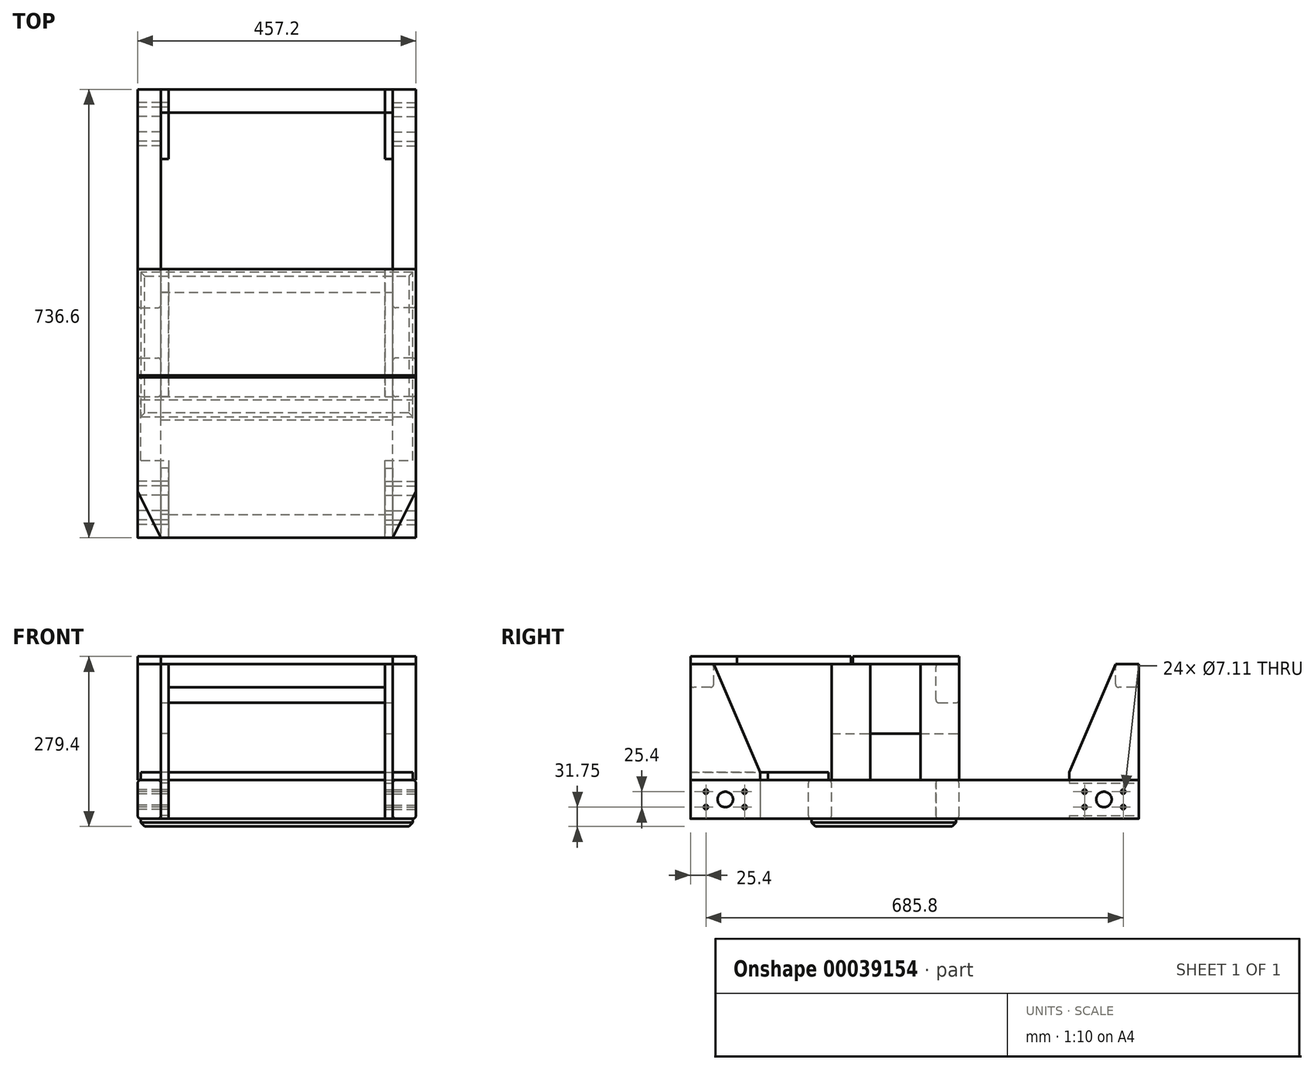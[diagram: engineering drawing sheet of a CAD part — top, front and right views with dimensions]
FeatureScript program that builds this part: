
annotation { "Feature Type Name" : "Feature", "Feature Type Description" : "" }
export const myFeature = defineFeature(function(context is Context, id is Id, definition is map)
    precondition{}
    {
        {
            var Q0;
            Q0=qCreatedBy(makeId("Front.planeOp"),FACE);
            var sketch = newSketch(context, id + "F0", { "sketchPlane" : qUnion([Q0])});
            skLineSegment(sketch, "E0", {"start": v(0, 25.4) * mm, "end": v(0, -25.4) * mm, "construction": true});
            skLineSegment(sketch, "E1.rect.bottom", {"start": v(-190.5, 31.75) * mm, "end": v(-228.6, 31.75) * mm});
            skLineSegment(sketch, "E1.rect.top", {"start": v(-190.5, -31.75) * mm, "end": v(-228.6, -31.75) * mm});
            skLineSegment(sketch, "E1.rect.left", {"start": v(-190.5, 31.75) * mm, "end": v(-190.5, -31.75) * mm});
            skLineSegment(sketch, "E1.rect.right", {"start": v(-228.6, 31.75) * mm, "end": v(-228.6, -31.75) * mm});
            skPoint(sketch, "E1.rect.middle", {"position": v(-209.55, 0) * mm});
            skLineSegment(sketch, "E2.MirrorCS", {"start": v(190.5, 31.75) * mm, "end": v(228.6, 31.75) * mm});
            skLineSegment(sketch, "E3.MirrorCS", {"start": v(190.5, -31.75) * mm, "end": v(228.6, -31.75) * mm});
            skLineSegment(sketch, "E4.MirrorCS", {"start": v(228.6, 31.75) * mm, "end": v(228.6, -31.75) * mm});
            skLineSegment(sketch, "E5.MirrorCS", {"start": v(190.5, 31.75) * mm, "end": v(190.5, -31.75) * mm});
            skPoint(sketch, "E6.MirrorP", {"position": v(209.55, 0) * mm});
            skSolve(sketch);
        }
        {
            var Q0;
            Q0=makeQuery(id+"F0.imprint","IMPRINT",FACE,{"disambiguationData":[TD([[makeQuery(id+"F0.imprint","IMPRINT",EDGE,{"derivedFrom":sQuery(id+"F0.wireOp",EDGE,"E1.rect.bottom")}),1.0]])]});
            extrude(context, id + "F1", {"entities" : qUnion([Q0]), "endBound" : BoundingType.SYMMETRIC, "depth" : 736.6 * mm});
        }
        {
            var Q0;
            Q0=makeQuery(id+"F1.opExtrude","SWEPT_FACE",FACE,{"disambiguationData":[OSD([sQuery(id+"F0.wireOp",EDGE,"E1.rect.right")])]});
            var sketch = newSketch(context, id + "F2", { "sketchPlane" : qUnion([Q0])});
            skLineSegment(sketch, "E7.rect.bottom", {"start": v(342.9, -12.7) * mm, "end": v(279.4, -12.7) * mm, "construction": true});
            skLineSegment(sketch, "E7.rect.top", {"start": v(342.9, 12.7) * mm, "end": v(279.4, 12.7) * mm, "construction": true});
            skLineSegment(sketch, "E7.rect.left", {"start": v(342.9, -12.7) * mm, "end": v(342.9, 12.7) * mm, "construction": true});
            skLineSegment(sketch, "E7.rect.right", {"start": v(279.4, -12.7) * mm, "end": v(279.4, 12.7) * mm, "construction": true});
            skPoint(sketch, "E7.rect.middle", {"position": v(311.15, 0) * mm});
            skCircle(sketch, "E8", {"center": v(311.15, 0) * mm, "radius": 12.7 * mm});
            skCircle(sketch, "E9", {"center": v(279.4, 12.7) * mm, "radius": 3.56 * mm});
            skCircle(sketch, "E10", {"center": v(279.4, -12.7) * mm, "radius": 3.56 * mm});
            skCircle(sketch, "E11", {"center": v(342.9, -12.7) * mm, "radius": 3.56 * mm});
            skCircle(sketch, "E12", {"center": v(342.9, 12.7) * mm, "radius": 3.56 * mm});
            skLineSegment(sketch, "E13", {"start": v(0, 31.75) * mm, "end": v(0, -31.75) * mm, "construction": true});
            skCircle(sketch, "E14.MirrorC", {"center": v(-342.9, 12.7) * mm, "radius": 3.56 * mm});
            skCircle(sketch, "E15.MirrorC", {"center": v(-342.9, -12.7) * mm, "radius": 3.56 * mm});
            skCircle(sketch, "E16.MirrorC", {"center": v(-279.4, 12.7) * mm, "radius": 3.56 * mm});
            skCircle(sketch, "E17.MirrorC", {"center": v(-279.4, -12.7) * mm, "radius": 3.56 * mm});
            skCircle(sketch, "E18.MirrorC", {"center": v(-311.15, 0) * mm, "radius": 12.7 * mm});
            skSolve(sketch);
        }
        {
            var Q0;
            Q0=qSketchRegion(id+"F2",true);
            extrude(context, id + "F3", {"entities" : qUnion([Q0]), "operationType" : NewBodyOperationType.REMOVE, "endBound" : BoundingType.THROUGH_ALL, "oppositeDirection" : true, "depth" : 25.4 * mm});
        }
        {
            var Q0;
            Q0=makeQuery(id+"F1.opExtrude","SWEPT_EDGE",EDGE,{"disambiguationData":[OSD([sQuery(id+"F0.wireOp",EDGE,"E1.rect.bottom"),sQuery(id+"F0.wireOp",EDGE,"E1.rect.right")])]});
            var Q1;
            Q1=makeQuery(id+"F1.opExtrude","SWEPT_EDGE",EDGE,{"disambiguationData":[OSD([sQuery(id+"F0.wireOp",EDGE,"E1.rect.bottom"),sQuery(id+"F0.wireOp",EDGE,"E1.rect.left")])]});
            var Q2;
            Q2=makeQuery(id+"F1.opExtrude","SWEPT_EDGE",EDGE,{"disambiguationData":[OSD([sQuery(id+"F0.wireOp",EDGE,"E1.rect.top"),sQuery(id+"F0.wireOp",EDGE,"E1.rect.right")])]});
            var Q3;
            Q3=makeQuery(id+"F1.opExtrude","SWEPT_EDGE",EDGE,{"disambiguationData":[OSD([sQuery(id+"F0.wireOp",EDGE,"E1.rect.top"),sQuery(id+"F0.wireOp",EDGE,"E1.rect.left")])]});
            fillet(context, id + "F4", {"entities" : qUnion([Q0, Q1, Q2, Q3]), "radius" : 5.08 * mm, "tangentPropagation" : true, "allowEdgeOverflow" : false});
        }
        {
            var Q0;
            Q0=makeQuery(id+"F1.opExtrude","SWEPT_BODY",BODY,{"disambiguationData":[OSD([sQuery(id+"F0.wireOp",EDGE,"E1.rect.bottom"),sQuery(id+"F0.wireOp",EDGE,"E1.rect.top"),sQuery(id+"F0.wireOp",EDGE,"E1.rect.left"),sQuery(id+"F0.wireOp",EDGE,"E1.rect.right")])]});
            var Q1;
            Q1=qCreatedBy(makeId("Right.planeOp"),FACE);
            mirror(context, id + "F5", {"entities" : qUnion([Q0]), "mirrorPlane" : qUnion([Q1])});
        }
        {
            var Q0;
            Q0=makeQuery(id+"F1.opExtrude","SWEPT_FACE",FACE,{"disambiguationData":[OSD([sQuery(id+"F0.wireOp",EDGE,"E1.rect.bottom")])]});
            var sketch = newSketch(context, id + "F6", { "sketchPlane" : qUnion([Q0])});
            skLineSegment(sketch, "E19.bottom", {"start": v(-190.5, -174.62) * mm, "end": v(190.5, -174.62) * mm});
            skLineSegment(sketch, "E19.top", {"start": v(-190.5, -136.53) * mm, "end": v(190.5, -136.53) * mm});
            skLineSegment(sketch, "E19.left", {"start": v(-190.5, -174.62) * mm, "end": v(-190.5, -136.53) * mm});
            skLineSegment(sketch, "E19.right", {"start": v(190.5, -174.62) * mm, "end": v(190.5, -136.53) * mm});
            skLineSegment(sketch, "E20", {"start": v(-190.5, -50.8) * mm, "end": v(190.5, -50.8) * mm, "construction": true});
            skLineSegment(sketch, "E21.MirrorCS", {"start": v(-190.5, 73.02) * mm, "end": v(190.5, 73.02) * mm});
            skLineSegment(sketch, "E22.MirrorCS", {"start": v(-190.5, 34.92) * mm, "end": v(190.5, 34.92) * mm});
            skLineSegment(sketch, "E23.MirrorCS", {"start": v(190.5, 73.02) * mm, "end": v(190.5, 34.92) * mm});
            skLineSegment(sketch, "E24.MirrorCS", {"start": v(-190.5, 73.02) * mm, "end": v(-190.5, 34.92) * mm});
            skSolve(sketch);
        }
        {
            var Q0;
            Q0=qSketchRegion(id+"F6",true);
            var Q1;
            Q1=makeQuery(id+"F5.opPattern","COPY",FACE,{"derivedFrom":makeQuery(id+"F1.opExtrude","SWEPT_FACE",FACE,{"disambiguationData":[OSD([sQuery(id+"F0.wireOp",EDGE,"E1.rect.top")])]}),"instanceName":"1"});
            extrude(context, id + "F7", {"entities" : qUnion([Q0]), "endBound" : BoundingType.UP_TO_SURFACE, "oppositeDirection" : true, "endBoundEntityFace" : qUnion([Q1]), "depth" : 25.4 * mm});
        }
        {
            var Q0;
            Q0=makeQuery(id+"F7.opExtrude","CAP_EDGE",EDGE,{"disambiguationData":[OSD([sQuery(id+"F6.wireOp",EDGE,"E21.MirrorCS")])],"isStart":false});
            var Q1;
            Q1=makeQuery(id+"F7.opExtrude","CAP_EDGE",EDGE,{"disambiguationData":[OSD([sQuery(id+"F6.wireOp",EDGE,"E22.MirrorCS")])],"isStart":false});
            var Q2;
            Q2=makeQuery(id+"F7.opExtrude","CAP_EDGE",EDGE,{"disambiguationData":[OSD([sQuery(id+"F6.wireOp",EDGE,"E19.top")])],"isStart":false});
            var Q3;
            Q3=makeQuery(id+"F7.opExtrude","CAP_EDGE",EDGE,{"disambiguationData":[OSD([sQuery(id+"F6.wireOp",EDGE,"E19.bottom")])],"isStart":false});
            var Q4;
            Q4=makeQuery(id+"F7.opExtrude","CAP_EDGE",EDGE,{"disambiguationData":[OSD([sQuery(id+"F6.wireOp",EDGE,"E19.bottom")])],"isStart":true});
            var Q5;
            Q5=makeQuery(id+"F7.opExtrude","CAP_EDGE",EDGE,{"disambiguationData":[OSD([sQuery(id+"F6.wireOp",EDGE,"E19.top")])],"isStart":true});
            var Q6;
            Q6=makeQuery(id+"F7.opExtrude","CAP_EDGE",EDGE,{"disambiguationData":[OSD([sQuery(id+"F6.wireOp",EDGE,"E22.MirrorCS")])],"isStart":true});
            var Q7;
            Q7=makeQuery(id+"F7.opExtrude","CAP_EDGE",EDGE,{"disambiguationData":[OSD([sQuery(id+"F6.wireOp",EDGE,"E21.MirrorCS")])],"isStart":true});
            fillet(context, id + "F8", {"entities" : qUnion([Q0, Q1, Q2, Q3, Q4, Q5, Q6, Q7]), "radius" : 5.08 * mm, "tangentPropagation" : true, "allowEdgeOverflow" : false});
        }
        {
            var Q0;
            Q0=makeQuery(id+"F1.opExtrude","SWEPT_FACE",FACE,{"disambiguationData":[OSD([sQuery(id+"F0.wireOp",EDGE,"E1.rect.bottom")])]});
            var sketch = newSketch(context, id + "F9", { "sketchPlane" : qUnion([Q0])});
            skLineSegment(sketch, "E25.bottom", {"start": v(-223.52, -241.3) * mm, "end": v(-177.8, -241.3) * mm});
            skLineSegment(sketch, "E25.top", {"start": v(-223.52, -141.6) * mm, "end": v(223.52, -141.6) * mm});
            skLineSegment(sketch, "E25.left", {"start": v(-223.52, -241.3) * mm, "end": v(-223.52, -141.6) * mm});
            skLineSegment(sketch, "E25.right", {"start": v(223.52, -241.3) * mm, "end": v(223.52, -141.6) * mm});
            skLineSegment(sketch, "E26.0", {"start": v(190.5, -141.6) * mm, "end": v(-190.5, -141.6) * mm, "construction": true});
            skLineSegment(sketch, "E27", {"start": v(-177.8, -241.3) * mm, "end": v(-177.8, -368.3) * mm});
            skLineSegment(sketch, "E28", {"start": v(-177.8, -368.3) * mm, "end": v(177.8, -368.3) * mm});
            skLineSegment(sketch, "E29", {"start": v(177.8, -368.3) * mm, "end": v(177.8, -241.3) * mm});
            skLineSegment(sketch, "E30", {"start": v(0, -141.6) * mm, "end": v(0, -368.3) * mm, "construction": true});
            skLineSegment(sketch, "E31.trimOffspring", {"start": v(177.8, -241.3) * mm, "end": v(223.52, -241.3) * mm});
            skSolve(sketch);
        }
        {
            var Q0;
            Q0=qSketchRegion(id+"F9",true);
            extrude(context, id + "F10", {"entities" : qUnion([Q0]), "depth" : 12.7 * mm});
        }
        {
            var Q0;
            Q0=makeQuery(id+"F5.opPattern","COPY",FACE,{"derivedFrom":makeQuery(id+"F1.opExtrude","SWEPT_FACE",FACE,{"disambiguationData":[OSD([sQuery(id+"F0.wireOp",EDGE,"E1.rect.top")])]}),"instanceName":"1"});
            var sketch = newSketch(context, id + "F11", { "sketchPlane" : qUnion([Q0])});
            skLineSegment(sketch, "E32.bottom", {"start": v(223.52, 169.55) * mm, "end": v(-223.52, 169.54) * mm});
            skLineSegment(sketch, "E32.top", {"start": v(223.52, -67.94) * mm, "end": v(-223.52, -67.95) * mm});
            skLineSegment(sketch, "E32.left", {"start": v(223.52, 169.55) * mm, "end": v(223.52, -67.94) * mm});
            skLineSegment(sketch, "E32.right", {"start": v(-223.52, 169.54) * mm, "end": v(-223.52, -67.95) * mm});
            skSolve(sketch);
        }
        {
            var Q0;
            Q0=qSketchRegion(id+"F11",true);
            extrude(context, id + "F12", {"entities" : qUnion([Q0]), "depth" : 12.7 * mm});
        }
        {
            var Q0;
            Q0=makeQuery(id+"F12.opExtrude","CAP_EDGE",EDGE,{"disambiguationData":[OSD([sQuery(id+"F11.wireOp",EDGE,"E32.top")])],"isStart":false});
            var Q1;
            Q1=makeQuery(id+"F12.opExtrude","CAP_EDGE",EDGE,{"disambiguationData":[OSD([sQuery(id+"F11.wireOp",EDGE,"E32.left")])],"isStart":false});
            var Q2;
            Q2=makeQuery(id+"F12.opExtrude","CAP_EDGE",EDGE,{"disambiguationData":[OSD([sQuery(id+"F11.wireOp",EDGE,"E32.bottom")])],"isStart":false});
            var Q3;
            Q3=makeQuery(id+"F12.opExtrude","CAP_EDGE",EDGE,{"disambiguationData":[OSD([sQuery(id+"F11.wireOp",EDGE,"E32.right")])],"isStart":false});
            chamfer(context, id + "F13", {"entities" : qUnion([Q0, Q1, Q2, Q3]), "width" : 6.35 * mm, "tangentPropagation" : true});
        }
        {
            var Q0;
            Q0=makeQuery(id+"F1.opExtrude","SWEPT_FACE",FACE,{"disambiguationData":[OSD([sQuery(id+"F0.wireOp",EDGE,"E1.rect.left")])]});
            var sketch = newSketch(context, id + "F14", { "sketchPlane" : qUnion([Q0])});
            skLineSegment(sketch, "E33", {"start": v(-254, -31.75) * mm, "end": v(-368.3, -31.75) * mm});
            skPoint(sketch, "E33.endSnap0", {"position": v(-368.3, 0) * mm});
            skLineSegment(sketch, "E34", {"start": v(-368.3, -31.75) * mm, "end": v(-368.3, 222.25) * mm});
            skLineSegment(sketch, "E35", {"start": v(-368.3, 222.25) * mm, "end": v(-330.2, 222.25) * mm});
            skLineSegment(sketch, "E36", {"start": v(-330.2, 222.25) * mm, "end": v(-254, 44.45) * mm});
            skLineSegment(sketch, "E37", {"start": v(-254, 44.45) * mm, "end": v(-254, -31.75) * mm});
            skLineSegment(sketch, "E38", {"start": v(0, -26.67) * mm, "end": v(0, 26.67) * mm, "construction": true});
            skLineSegment(sketch, "E39.MirrorCS", {"start": v(368.3, 222.25) * mm, "end": v(330.2, 222.25) * mm});
            skLineSegment(sketch, "E40.MirrorCS", {"start": v(254, -31.75) * mm, "end": v(368.3, -31.75) * mm});
            skPoint(sketch, "E41.MirrorP", {"position": v(368.3, 0) * mm});
            skLineSegment(sketch, "E42.MirrorCS", {"start": v(330.2, 222.25) * mm, "end": v(254, 44.45) * mm});
            skLineSegment(sketch, "E43.MirrorCS", {"start": v(254, 44.45) * mm, "end": v(254, -31.75) * mm});
            skLineSegment(sketch, "E44.MirrorCS", {"start": v(368.3, -31.75) * mm, "end": v(368.3, 222.25) * mm});
            skSolve(sketch);
        }
        {
            var Q0;
            {var subQ6=sQuery(id+"F14.wireOp",EDGE,"E35");Q0=makeQuery(id+"F14.imprint","IMPRINT",FACE,{"disambiguationData":[TD([[makeQuery(id+"F14.imprint","IMPRINT",EDGE,{"derivedFrom":subQ6}),-1.0]])]});}
            var Q1;
            {var subQ0=sQuery(id+"F0.wireOp",EDGE,"E1.rect.left");var subQ1=makeQuery(id+"F1.opExtrude","SWEPT_FACE",FACE,{"disambiguationData":[OSD([subQ0])]});Q1=makeQuery(id+"F14.imprint","IMPRINT",FACE,{"disambiguationData":[TD([[makeQuery(id+"F14.imprint","IMPRINT",EDGE,{"derivedFrom":makeQuery(id+"F3.boolean.opBoolean","INTERSECT",EDGE,{"derivedFrom":[subQ1,makeQuery(id+"F3.opExtrude","SWEPT_FACE",FACE,{"disambiguationData":[OSD([sQuery(id+"F2.wireOp",EDGE,"E8")])]})]})}),-1.0]])]});}
            var Q2;
            {var subQ4=sQuery(id+"F14.wireOp",EDGE,"E33");Q2=makeQuery(id+"F14.imprint","IMPRINT",FACE,{"disambiguationData":[TD([[makeQuery(id+"F14.imprint","IMPRINT",EDGE,{"derivedFrom":subQ4}),-1.0]])]});}
            var Q3;
            {var subQ0=sQuery(id+"F14.wireOp",EDGE,"E39.MirrorCS");Q3=makeQuery(id+"F14.imprint","IMPRINT",FACE,{"disambiguationData":[TD([[makeQuery(id+"F14.imprint","IMPRINT",EDGE,{"derivedFrom":subQ0}),1.0]])]});}
            var Q4;
            {var subQ0=sQuery(id+"F0.wireOp",EDGE,"E1.rect.left");var subQ1=makeQuery(id+"F1.opExtrude","SWEPT_FACE",FACE,{"disambiguationData":[OSD([subQ0])]});Q4=makeQuery(id+"F14.imprint","IMPRINT",FACE,{"disambiguationData":[TD([[makeQuery(id+"F14.imprint","IMPRINT",EDGE,{"derivedFrom":makeQuery(id+"F3.boolean.opBoolean","INTERSECT",EDGE,{"derivedFrom":[subQ1,makeQuery(id+"F3.opExtrude","SWEPT_FACE",FACE,{"disambiguationData":[OSD([sQuery(id+"F2.wireOp",EDGE,"E14.MirrorC")])]})]})}),1.0]])]});}
            var Q5;
            {var subQ6=sQuery(id+"F14.wireOp",EDGE,"E40.MirrorCS");Q5=makeQuery(id+"F14.imprint","IMPRINT",FACE,{"disambiguationData":[TD([[makeQuery(id+"F14.imprint","IMPRINT",EDGE,{"derivedFrom":subQ6}),1.0]])]});}
            extrude(context, id + "F15", {"entities" : qUnion([Q0, Q1, Q2, Q3, Q4, Q5]), "depth" : 12.7 * mm});
        }
        {
            var Q0;
            Q0=makeQuery(id+"F1.opExtrude","SWEPT_FACE",FACE,{"disambiguationData":[OSD([sQuery(id+"F0.wireOp",EDGE,"E1.rect.bottom")])]});
            var sketch = newSketch(context, id + "F16", { "sketchPlane" : qUnion([Q0])});
            skLineSegment(sketch, "E45.bottom", {"start": v(-228.6, 73.02) * mm, "end": v(-190.5, 73.02) * mm});
            skLineSegment(sketch, "E45.top", {"start": v(-228.6, 9.52) * mm, "end": v(-190.5, 9.52) * mm});
            skLineSegment(sketch, "E45.left", {"start": v(-228.6, 73.02) * mm, "end": v(-228.6, 9.52) * mm});
            skLineSegment(sketch, "E45.right", {"start": v(-190.5, 73.02) * mm, "end": v(-190.5, 9.52) * mm});
            skLineSegment(sketch, "E46.bottom", {"start": v(-228.6, -136.53) * mm, "end": v(-190.5, -136.53) * mm});
            skLineSegment(sketch, "E46.top", {"start": v(-228.6, -73.03) * mm, "end": v(-190.5, -73.03) * mm});
            skLineSegment(sketch, "E46.left", {"start": v(-228.6, -136.53) * mm, "end": v(-228.6, -73.03) * mm});
            skLineSegment(sketch, "E46.right", {"start": v(-190.5, -136.53) * mm, "end": v(-190.5, -73.03) * mm});
            skSolve(sketch);
        }
        {
            var Q0;
            Q0=qSketchRegion(id+"F16",true);
            var Q1;
            Q1=makeQuery(id+"F15.opExtrude","SWEPT_FACE",FACE,{"disambiguationData":[OSD([sQuery(id+"F14.wireOp",EDGE,"E35")])]});
            extrude(context, id + "F17", {"entities" : qUnion([Q0]), "endBound" : BoundingType.UP_TO_SURFACE, "endBoundEntityFace" : qUnion([Q1]), "depth" : 25.4 * mm});
        }
        {
            var Q0;
            Q0=makeQuery(id+"F1.opExtrude","SWEPT_FACE",FACE,{"disambiguationData":[OSD([sQuery(id+"F0.wireOp",EDGE,"E1.rect.left")])]});
            var sketch = newSketch(context, id + "F18", { "sketchPlane" : qUnion([Q0])});
            skLineSegment(sketch, "E47", {"start": v(-136.53, -31.75) * mm, "end": v(-136.53, 107.95) * mm});
            skLineSegment(sketch, "E48", {"start": v(-136.53, 107.95) * mm, "end": v(73.02, 107.95) * mm});
            skLineSegment(sketch, "E49", {"start": v(73.02, 107.95) * mm, "end": v(73.02, 31.75) * mm});
            skLineSegment(sketch, "E50", {"start": v(73.02, 31.75) * mm, "end": v(34.92, 31.75) * mm});
            skLineSegment(sketch, "E51", {"start": v(34.92, 31.75) * mm, "end": v(34.92, -31.75) * mm});
            skLineSegment(sketch, "E52", {"start": v(34.92, -31.75) * mm, "end": v(-136.53, -31.75) * mm});
            skSolve(sketch);
        }
        {
            var Q0;
            Q0=qSketchRegion(id+"F18",true);
            extrude(context, id + "F19", {"entities" : qUnion([Q0]), "depth" : 12.7 * mm});
        }
        {
            var Q0;
            Q0=makeQuery(id+"F15.opExtrude","SWEPT_BODY",BODY,{"disambiguationData":[OSD([sQuery(id+"F0.wireOp",EDGE,"E1.rect.left"),sQuery(id+"F2.wireOp",EDGE,"E8"),sQuery(id+"F2.wireOp",EDGE,"E9"),sQuery(id+"F2.wireOp",EDGE,"E10"),sQuery(id+"F2.wireOp",EDGE,"E11"),sQuery(id+"F2.wireOp",EDGE,"E12"),sQuery(id+"F14.wireOp",EDGE,"E33"),sQuery(id+"F14.wireOp",EDGE,"E34"),sQuery(id+"F14.wireOp",EDGE,"E35"),sQuery(id+"F14.wireOp",EDGE,"E36"),sQuery(id+"F14.wireOp",EDGE,"E37")])]});
            var Q1;
            Q1=makeQuery(id+"F17.opExtrude","SWEPT_BODY",BODY,{"disambiguationData":[OSD([sQuery(id+"F16.wireOp",EDGE,"E46.bottom"),sQuery(id+"F16.wireOp",EDGE,"E46.top"),sQuery(id+"F16.wireOp",EDGE,"E46.left"),sQuery(id+"F16.wireOp",EDGE,"E46.right")])]});
            var Q2;
            Q2=makeQuery(id+"F19.opExtrude","SWEPT_BODY",BODY,{"disambiguationData":[OSD([sQuery(id+"F18.wireOp",EDGE,"E47"),sQuery(id+"F18.wireOp",EDGE,"E48"),sQuery(id+"F18.wireOp",EDGE,"E49"),sQuery(id+"F18.wireOp",EDGE,"E50"),sQuery(id+"F18.wireOp",EDGE,"E51"),sQuery(id+"F18.wireOp",EDGE,"E52")])]});
            var Q3;
            Q3=makeQuery(id+"F17.opExtrude","SWEPT_BODY",BODY,{"disambiguationData":[OSD([sQuery(id+"F16.wireOp",EDGE,"E45.bottom"),sQuery(id+"F16.wireOp",EDGE,"E45.top"),sQuery(id+"F16.wireOp",EDGE,"E45.left"),sQuery(id+"F16.wireOp",EDGE,"E45.right")])]});
            var Q4;
            Q4=makeQuery(id+"F15.opExtrude","SWEPT_BODY",BODY,{"disambiguationData":[OSD([sQuery(id+"F0.wireOp",EDGE,"E1.rect.left"),sQuery(id+"F2.wireOp",EDGE,"E14.MirrorC"),sQuery(id+"F2.wireOp",EDGE,"E15.MirrorC"),sQuery(id+"F2.wireOp",EDGE,"E16.MirrorC"),sQuery(id+"F2.wireOp",EDGE,"E17.MirrorC"),sQuery(id+"F2.wireOp",EDGE,"E18.MirrorC"),sQuery(id+"F14.wireOp",EDGE,"E39.MirrorCS"),sQuery(id+"F14.wireOp",EDGE,"E40.MirrorCS"),sQuery(id+"F14.wireOp",EDGE,"E42.MirrorCS"),sQuery(id+"F14.wireOp",EDGE,"E43.MirrorCS"),sQuery(id+"F14.wireOp",EDGE,"E44.MirrorCS")])]});
            var Q5;
            Q5=qCreatedBy(makeId("Right.planeOp"),FACE);
            mirror(context, id + "F20", {"entities" : qUnion([Q0, Q1, Q2, Q3, Q4]), "mirrorPlane" : qUnion([Q5])});
        }
        {
            var Q0;
            Q0=makeQuery(id+"F20.opPattern","COPY",FACE,{"derivedFrom":makeQuery(id+"F15.opExtrude","CAP_FACE",FACE,{"disambiguationData":[OSD([sQuery(id+"F0.wireOp",EDGE,"E1.rect.left"),sQuery(id+"F2.wireOp",EDGE,"E14.MirrorC"),sQuery(id+"F2.wireOp",EDGE,"E15.MirrorC"),sQuery(id+"F2.wireOp",EDGE,"E16.MirrorC"),sQuery(id+"F2.wireOp",EDGE,"E17.MirrorC"),sQuery(id+"F2.wireOp",EDGE,"E18.MirrorC"),sQuery(id+"F14.wireOp",EDGE,"E39.MirrorCS"),sQuery(id+"F14.wireOp",EDGE,"E40.MirrorCS"),sQuery(id+"F14.wireOp",EDGE,"E42.MirrorCS"),sQuery(id+"F14.wireOp",EDGE,"E43.MirrorCS"),sQuery(id+"F14.wireOp",EDGE,"E44.MirrorCS")])],"isStart":false}),"instanceName":"1"});
            var sketch = newSketch(context, id + "F21", { "sketchPlane" : qUnion([Q0])});
            skLineSegment(sketch, "E53.bottom", {"start": v(-330.2, 222.25) * mm, "end": v(-368.3, 222.25) * mm});
            skLineSegment(sketch, "E53.top", {"start": v(-330.2, 184.15) * mm, "end": v(-368.3, 184.15) * mm});
            skLineSegment(sketch, "E53.left", {"start": v(-330.2, 222.25) * mm, "end": v(-330.2, 184.15) * mm});
            skLineSegment(sketch, "E53.right", {"start": v(-368.3, 222.25) * mm, "end": v(-368.3, 184.15) * mm});
            skLineSegment(sketch, "E54.bottom", {"start": v(368.3, 222.25) * mm, "end": v(330.2, 222.25) * mm});
            skLineSegment(sketch, "E54.top", {"start": v(368.3, 184.15) * mm, "end": v(330.2, 184.15) * mm});
            skLineSegment(sketch, "E54.left", {"start": v(368.3, 222.25) * mm, "end": v(368.3, 184.15) * mm});
            skLineSegment(sketch, "E54.right", {"start": v(330.2, 222.25) * mm, "end": v(330.2, 184.15) * mm});
            skSolve(sketch);
        }
        {
            var Q0;
            Q0=qSketchRegion(id+"F21",true);
            var Q1;
            Q1=makeQuery(id+"F15.opExtrude","CAP_FACE",FACE,{"disambiguationData":[OSD([sQuery(id+"F0.wireOp",EDGE,"E1.rect.left"),sQuery(id+"F2.wireOp",EDGE,"E14.MirrorC"),sQuery(id+"F2.wireOp",EDGE,"E15.MirrorC"),sQuery(id+"F2.wireOp",EDGE,"E16.MirrorC"),sQuery(id+"F2.wireOp",EDGE,"E17.MirrorC"),sQuery(id+"F2.wireOp",EDGE,"E18.MirrorC"),sQuery(id+"F14.wireOp",EDGE,"E39.MirrorCS"),sQuery(id+"F14.wireOp",EDGE,"E40.MirrorCS"),sQuery(id+"F14.wireOp",EDGE,"E42.MirrorCS"),sQuery(id+"F14.wireOp",EDGE,"E43.MirrorCS"),sQuery(id+"F14.wireOp",EDGE,"E44.MirrorCS")])],"isStart":false});
            extrude(context, id + "F22", {"entities" : qUnion([Q0]), "endBound" : BoundingType.UP_TO_SURFACE, "endBoundEntityFace" : qUnion([Q1]), "depth" : 25.4 * mm});
        }
        {
            var Q0;
            Q0=makeQuery(id+"F20.opPattern","COPY",FACE,{"derivedFrom":makeQuery(id+"F17.opExtrude","SWEPT_FACE",FACE,{"disambiguationData":[OSD([sQuery(id+"F16.wireOp",EDGE,"E45.right")])]}),"instanceName":"1"});
            var sketch = newSketch(context, id + "F23", { "sketchPlane" : qUnion([Q0])});
            skLineSegment(sketch, "E55.bottom", {"start": v(-73.02, 222.25) * mm, "end": v(-34.92, 222.25) * mm});
            skLineSegment(sketch, "E55.top", {"start": v(-73.02, 158.75) * mm, "end": v(-34.92, 158.75) * mm});
            skLineSegment(sketch, "E55.left", {"start": v(-73.02, 222.25) * mm, "end": v(-73.02, 158.75) * mm});
            skLineSegment(sketch, "E55.right", {"start": v(-34.92, 222.25) * mm, "end": v(-34.92, 158.75) * mm});
            skSolve(sketch);
        }
        {
            var Q0;
            Q0=qSketchRegion(id+"F23",true);
            var Q1;
            Q1=makeQuery(id+"F17.opExtrude","SWEPT_FACE",FACE,{"disambiguationData":[OSD([sQuery(id+"F16.wireOp",EDGE,"E45.right")])]});
            extrude(context, id + "F24", {"entities" : qUnion([Q0]), "endBound" : BoundingType.UP_TO_SURFACE, "endBoundEntityFace" : qUnion([Q1]), "depth" : 25.4 * mm});
        }
        {
            var Q0;
            Q0=makeQuery(id+"F22.opExtrude","SWEPT_EDGE",EDGE,{"disambiguationData":[OSD([sQuery(id+"F14.wireOp",EDGE,"E42.MirrorCS"),sQuery(id+"F21.wireOp",EDGE,"E53.bottom"),sQuery(id+"F21.wireOp",EDGE,"E53.left")])]});
            var Q1;
            Q1=makeQuery(id+"F22.opExtrude","SWEPT_EDGE",EDGE,{"disambiguationData":[OSD([sQuery(id+"F21.wireOp",EDGE,"E53.bottom"),sQuery(id+"F21.wireOp",EDGE,"E53.right")])]});
            var Q2;
            Q2=makeQuery(id+"F22.opExtrude","SWEPT_EDGE",EDGE,{"disambiguationData":[OSD([sQuery(id+"F21.wireOp",EDGE,"E53.top"),sQuery(id+"F21.wireOp",EDGE,"E53.left")])]});
            var Q3;
            Q3=makeQuery(id+"F22.opExtrude","SWEPT_EDGE",EDGE,{"disambiguationData":[OSD([sQuery(id+"F14.wireOp",EDGE,"E44.MirrorCS"),sQuery(id+"F21.wireOp",EDGE,"E53.top"),sQuery(id+"F21.wireOp",EDGE,"E53.right")])]});
            var Q4;
            Q4=makeQuery(id+"F24.opExtrude","SWEPT_EDGE",EDGE,{"disambiguationData":[OSD([sQuery(id+"F23.wireOp",EDGE,"E55.bottom"),sQuery(id+"F23.wireOp",EDGE,"E55.left")])]});
            var Q5;
            Q5=makeQuery(id+"F24.opExtrude","SWEPT_EDGE",EDGE,{"disambiguationData":[OSD([sQuery(id+"F16.wireOp",EDGE,"E45.bottom"),sQuery(id+"F16.wireOp",EDGE,"E45.right"),sQuery(id+"F23.wireOp",EDGE,"E55.top"),sQuery(id+"F23.wireOp",EDGE,"E55.left")])]});
            var Q6;
            Q6=makeQuery(id+"F24.opExtrude","SWEPT_EDGE",EDGE,{"disambiguationData":[OSD([sQuery(id+"F16.wireOp",EDGE,"E45.right"),sQuery(id+"F23.wireOp",EDGE,"E55.bottom"),sQuery(id+"F23.wireOp",EDGE,"E55.right")])]});
            var Q7;
            Q7=makeQuery(id+"F24.opExtrude","SWEPT_EDGE",EDGE,{"disambiguationData":[OSD([sQuery(id+"F23.wireOp",EDGE,"E55.top"),sQuery(id+"F23.wireOp",EDGE,"E55.right")])]});
            var Q8;
            Q8=makeQuery(id+"F17.opExtrude","SWEPT_EDGE",EDGE,{"disambiguationData":[OSD([sQuery(id+"F16.wireOp",EDGE,"E45.top"),sQuery(id+"F16.wireOp",EDGE,"E45.right")])]});
            var Q9;
            Q9=makeQuery(id+"F17.opExtrude","SWEPT_EDGE",EDGE,{"disambiguationData":[OSD([sQuery(id+"F16.wireOp",EDGE,"E45.top"),sQuery(id+"F16.wireOp",EDGE,"E45.left")])]});
            var Q10;
            Q10=makeQuery(id+"F17.opExtrude","SWEPT_EDGE",EDGE,{"disambiguationData":[OSD([sQuery(id+"F16.wireOp",EDGE,"E45.bottom"),sQuery(id+"F16.wireOp",EDGE,"E45.left")])]});
            var Q11;
            Q11=makeQuery(id+"F17.opExtrude","SWEPT_EDGE",EDGE,{"disambiguationData":[OSD([sQuery(id+"F16.wireOp",EDGE,"E45.bottom"),sQuery(id+"F16.wireOp",EDGE,"E45.right")])]});
            var Q12;
            Q12=makeQuery(id+"F17.opExtrude","SWEPT_EDGE",EDGE,{"disambiguationData":[OSD([sQuery(id+"F16.wireOp",EDGE,"E46.top"),sQuery(id+"F16.wireOp",EDGE,"E46.right")])]});
            var Q13;
            Q13=makeQuery(id+"F17.opExtrude","SWEPT_EDGE",EDGE,{"disambiguationData":[OSD([sQuery(id+"F16.wireOp",EDGE,"E46.top"),sQuery(id+"F16.wireOp",EDGE,"E46.left")])]});
            var Q14;
            Q14=makeQuery(id+"F17.opExtrude","SWEPT_EDGE",EDGE,{"disambiguationData":[OSD([sQuery(id+"F16.wireOp",EDGE,"E46.bottom"),sQuery(id+"F16.wireOp",EDGE,"E46.left")])]});
            var Q15;
            Q15=makeQuery(id+"F17.opExtrude","SWEPT_EDGE",EDGE,{"disambiguationData":[OSD([sQuery(id+"F16.wireOp",EDGE,"E46.bottom"),sQuery(id+"F16.wireOp",EDGE,"E46.right")])]});
            var Q16;
            Q16=makeQuery(id+"F20.opPattern","COPY",EDGE,{"derivedFrom":makeQuery(id+"F17.opExtrude","SWEPT_EDGE",EDGE,{"disambiguationData":[OSD([sQuery(id+"F16.wireOp",EDGE,"E46.bottom"),sQuery(id+"F16.wireOp",EDGE,"E46.right")])]}),"instanceName":"1"});
            var Q17;
            Q17=makeQuery(id+"F20.opPattern","COPY",EDGE,{"derivedFrom":makeQuery(id+"F17.opExtrude","SWEPT_EDGE",EDGE,{"disambiguationData":[OSD([sQuery(id+"F16.wireOp",EDGE,"E46.top"),sQuery(id+"F16.wireOp",EDGE,"E46.right")])]}),"instanceName":"1"});
            var Q18;
            Q18=makeQuery(id+"F20.opPattern","COPY",EDGE,{"derivedFrom":makeQuery(id+"F17.opExtrude","SWEPT_EDGE",EDGE,{"disambiguationData":[OSD([sQuery(id+"F16.wireOp",EDGE,"E46.bottom"),sQuery(id+"F16.wireOp",EDGE,"E46.left")])]}),"instanceName":"1"});
            var Q19;
            Q19=makeQuery(id+"F22.opExtrude","SWEPT_EDGE",EDGE,{"disambiguationData":[OSD([sQuery(id+"F21.wireOp",EDGE,"E54.bottom"),sQuery(id+"F21.wireOp",EDGE,"E54.left")])]});
            var Q20;
            Q20=makeQuery(id+"F22.opExtrude","SWEPT_EDGE",EDGE,{"disambiguationData":[OSD([sQuery(id+"F21.wireOp",EDGE,"E54.top"),sQuery(id+"F21.wireOp",EDGE,"E54.left")])]});
            var Q21;
            Q21=makeQuery(id+"F22.opExtrude","SWEPT_EDGE",EDGE,{"disambiguationData":[OSD([sQuery(id+"F21.wireOp",EDGE,"E54.bottom"),sQuery(id+"F21.wireOp",EDGE,"E54.right")])]});
            var Q22;
            Q22=makeQuery(id+"F22.opExtrude","SWEPT_EDGE",EDGE,{"disambiguationData":[OSD([sQuery(id+"F21.wireOp",EDGE,"E54.top"),sQuery(id+"F21.wireOp",EDGE,"E54.right")])]});
            var Q23;
            Q23=makeQuery(id+"F20.opPattern","COPY",EDGE,{"derivedFrom":makeQuery(id+"F17.opExtrude","SWEPT_EDGE",EDGE,{"disambiguationData":[OSD([sQuery(id+"F16.wireOp",EDGE,"E46.top"),sQuery(id+"F16.wireOp",EDGE,"E46.left")])]}),"instanceName":"1"});
            var Q24;
            Q24=makeQuery(id+"F20.opPattern","COPY",EDGE,{"derivedFrom":makeQuery(id+"F17.opExtrude","SWEPT_EDGE",EDGE,{"disambiguationData":[OSD([sQuery(id+"F16.wireOp",EDGE,"E45.bottom"),sQuery(id+"F16.wireOp",EDGE,"E45.left")])]}),"instanceName":"1"});
            var Q25;
            Q25=makeQuery(id+"F20.opPattern","COPY",EDGE,{"derivedFrom":makeQuery(id+"F17.opExtrude","SWEPT_EDGE",EDGE,{"disambiguationData":[OSD([sQuery(id+"F16.wireOp",EDGE,"E45.bottom"),sQuery(id+"F16.wireOp",EDGE,"E45.right")])]}),"instanceName":"1"});
            var Q26;
            Q26=makeQuery(id+"F20.opPattern","COPY",EDGE,{"derivedFrom":makeQuery(id+"F17.opExtrude","SWEPT_EDGE",EDGE,{"disambiguationData":[OSD([sQuery(id+"F16.wireOp",EDGE,"E45.top"),sQuery(id+"F16.wireOp",EDGE,"E45.left")])]}),"instanceName":"1"});
            var Q27;
            Q27=makeQuery(id+"F20.opPattern","COPY",EDGE,{"derivedFrom":makeQuery(id+"F17.opExtrude","SWEPT_EDGE",EDGE,{"disambiguationData":[OSD([sQuery(id+"F16.wireOp",EDGE,"E45.top"),sQuery(id+"F16.wireOp",EDGE,"E45.right")])]}),"instanceName":"1"});
            fillet(context, id + "F25", {"entities" : qUnion([Q0, Q1, Q2, Q3, Q4, Q5, Q6, Q7, Q8, Q9, Q10, Q11, Q12, Q13, Q14, Q15, Q16, Q17, Q18, Q19, Q20, Q21, Q22, Q23, Q24, Q25, Q26, Q27]), "radius" : 5.08 * mm, "tangentPropagation" : true, "allowEdgeOverflow" : false});
        }
        {
            var Q0;
            Q0=makeQuery(id+"F17.opExtrude","CAP_FACE",FACE,{"disambiguationData":[OSD([sQuery(id+"F16.wireOp",EDGE,"E46.bottom"),sQuery(id+"F16.wireOp",EDGE,"E46.top"),sQuery(id+"F16.wireOp",EDGE,"E46.left"),sQuery(id+"F16.wireOp",EDGE,"E46.right")])],"isStart":false});
            var sketch = newSketch(context, id + "F26", { "sketchPlane" : qUnion([Q0])});
            skLineSegment(sketch, "E56", {"start": v(228.6, -104.78) * mm, "end": v(228.6, -292.1) * mm});
            skLineSegment(sketch, "E57", {"start": v(228.6, -292.1) * mm, "end": v(190.5, -368.3) * mm});
            skLineSegment(sketch, "E58", {"start": v(190.5, -368.3) * mm, "end": v(-190.5, -368.3) * mm});
            skLineSegment(sketch, "E59", {"start": v(-190.5, -368.3) * mm, "end": v(-228.6, -292.1) * mm});
            skLineSegment(sketch, "E60", {"start": v(-228.6, -292.1) * mm, "end": v(-228.6, -104.78) * mm});
            skLineSegment(sketch, "E61", {"start": v(-228.6, -104.78) * mm, "end": v(228.6, -104.78) * mm});
            skSolve(sketch);
        }
        {
            var Q0;
            Q0=qSketchRegion(id+"F26",true);
            extrude(context, id + "F27", {"entities" : qUnion([Q0]), "depth" : 12.7 * mm});
        }
        {
            var Q0;
            Q0=makeQuery(id+"F20.opPattern","COPY",FACE,{"derivedFrom":makeQuery(id+"F17.opExtrude","CAP_FACE",FACE,{"disambiguationData":[OSD([sQuery(id+"F16.wireOp",EDGE,"E45.bottom"),sQuery(id+"F16.wireOp",EDGE,"E45.top"),sQuery(id+"F16.wireOp",EDGE,"E45.left"),sQuery(id+"F16.wireOp",EDGE,"E45.right")])],"isStart":false}),"instanceName":"1"});
            var sketch = newSketch(context, id + "F28", { "sketchPlane" : qUnion([Q0])});
            skLineSegment(sketch, "E62.bottom", {"start": v(228.6, 73.03) * mm, "end": v(-228.6, 73.02) * mm});
            skLineSegment(sketch, "E62.top", {"start": v(228.6, -101.6) * mm, "end": v(-228.6, -101.6) * mm});
            skLineSegment(sketch, "E62.left", {"start": v(228.6, 73.03) * mm, "end": v(228.6, -101.6) * mm});
            skLineSegment(sketch, "E62.right", {"start": v(-228.6, 73.02) * mm, "end": v(-228.6, -101.6) * mm});
            skSolve(sketch);
        }
        {
            var Q0;
            Q0=qSketchRegion(id+"F28",true);
            extrude(context, id + "F29", {"entities" : qUnion([Q0]), "depth" : 12.7 * mm});
        }
    });
